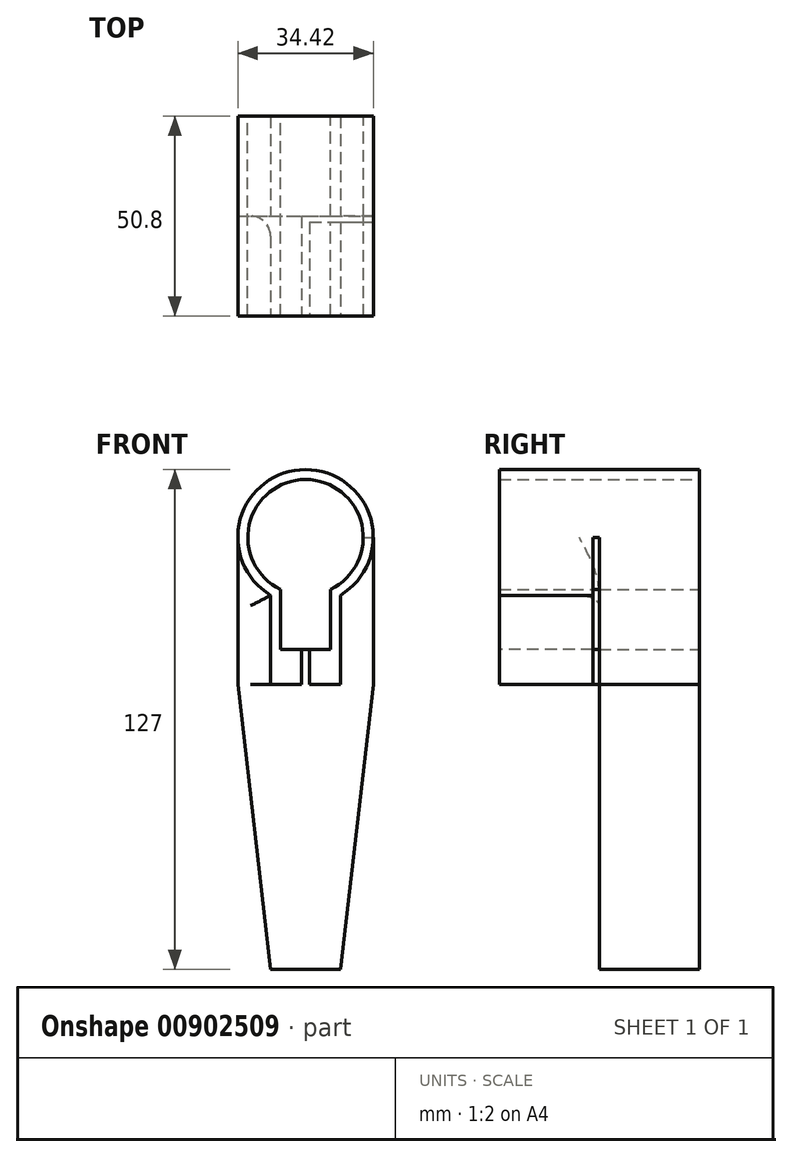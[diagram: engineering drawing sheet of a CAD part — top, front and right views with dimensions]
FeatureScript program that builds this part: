
annotation { "Feature Type Name" : "Feature", "Feature Type Description" : "" }
export const myFeature = defineFeature(function(context is Context, id is Id, definition is map)
    precondition{}
    {
        {
            var Q0;
            Q0=qCreatedBy(makeId("Front.planeOp"),FACE);
            var sketch = newSketch(context, id + "F0", { "sketchPlane" : qUnion([Q0])});
            skLineSegment(sketch, "E0.bottom", {"start": v(-17.2, 17.2) * mm, "end": v(17.2, 17.2) * mm});
            skLineSegment(sketch, "E0.top", {"start": v(-17.2, -109.8) * mm, "end": v(17.2, -109.8) * mm});
            skLineSegment(sketch, "E0.left", {"start": v(-17.2, 17.2) * mm, "end": v(-17.2, -109.8) * mm});
            skLineSegment(sketch, "E0.right", {"start": v(17.2, 17.2) * mm, "end": v(17.2, -109.8) * mm});
            skArc(sketch, "E1", {"start": v(6.35, -13.22) * mm, "mid": v(0, 14.67) * mm, "end": v(-6.35, -13.22) * mm});
            skLineSegment(sketch, "E2.top", {"start": v(-6.35, -28.5) * mm, "end": v(6.35, -28.5) * mm});
            skLineSegment(sketch, "E2.left", {"start": v(-6.35, -13.22) * mm, "end": v(-6.35, -28.5) * mm});
            skLineSegment(sketch, "E2.right", {"start": v(6.35, -13.22) * mm, "end": v(6.35, -28.5) * mm});
            skPoint(sketch, "E3", {"position": v(0, -28.5) * mm});
            skArc(sketch, "E4", {"start": v(6.35, -16) * mm, "mid": v(0, 17.2) * mm, "end": v(-6.35, -16) * mm});
            skSolve(sketch);
        }
        {
            var Q0;
            {var subQ4=sQuery(id+"F0.wireOp",EDGE,"E1");Q0=makeQuery(id+"F0.imprint","IMPRINT",FACE,{"disambiguationData":[TD([[makeQuery(id+"F0.imprint","IMPRINT",EDGE,{"derivedFrom":subQ4}),-1.0]])]});}
            var Q1;
            {var subQ2=sQuery(id+"F0.wireOp",EDGE,"E0.top");Q1=makeQuery(id+"F0.imprint","IMPRINT",FACE,{"disambiguationData":[TD([[makeQuery(id+"F0.imprint","IMPRINT",EDGE,{"derivedFrom":subQ2}),1.0]])]});}
            extrude(context, id + "F1", {"entities" : qUnion([Q0, Q1]), "depth" : 50.8 * mm, "offsetDistance" : 25.4 * mm});
        }
        {
            var Q0;
            Q0=makeQuery(id+"F1.opExtrude","CAP_FACE",FACE,{"disambiguationData":[OSD([sQuery(id+"F0.wireOp",EDGE,"E0.top"),sQuery(id+"F0.wireOp",EDGE,"E0.left"),sQuery(id+"F0.wireOp",EDGE,"E0.right"),sQuery(id+"F0.wireOp",EDGE,"E1"),sQuery(id+"F0.wireOp",EDGE,"E2.top"),sQuery(id+"F0.wireOp",EDGE,"E2.left"),sQuery(id+"F0.wireOp",EDGE,"E2.right"),sQuery(id+"F0.wireOp",EDGE,"E4")])],"isStart":false});
            var sketch = newSketch(context, id + "F2", { "sketchPlane" : qUnion([Q0])});
            skArc(sketch, "E5.0", {"start": v(6.35, -16) * mm, "mid": v(0, 17.2) * mm, "end": v(-6.35, -16) * mm});
            skLineSegment(sketch, "E6", {"start": v(-8.9, -14.73) * mm, "end": v(-8.9, -37.39) * mm});
            skLineSegment(sketch, "E7", {"start": v(-8.9, -37.39) * mm, "end": v(8.9, -37.39) * mm});
            skLineSegment(sketch, "E8", {"start": v(8.9, -37.39) * mm, "end": v(8.9, -14.73) * mm});
            skSolve(sketch);
        }
        {
            var Q0;
            {var subQ0=sQuery(id+"F2.wireOp",EDGE,"E6");Q0=makeQuery(id+"F2.imprint","IMPRINT",FACE,{"disambiguationData":[TD([[makeQuery(id+"F2.imprint","IMPRINT",EDGE,{"derivedFrom":subQ0}),-1.0]])]});}
            extrude(context, id + "F3", {"entities" : qUnion([Q0]), "operationType" : NewBodyOperationType.REMOVE, "oppositeDirection" : true, "depth" : 25.4 * mm, "offsetDistance" : 25.4 * mm});
        }
        {
            var Q0;
            Q0=makeQuery(id+"F1.opExtrude","SWEPT_FACE",FACE,{"disambiguationData":[OSD([sQuery(id+"F0.wireOp",EDGE,"E0.right")])]});
            var sketch = newSketch(context, id + "F4", { "sketchPlane" : qUnion([Q0])});
            skLineSegment(sketch, "E9.bottom", {"start": v(-25.4, 0) * mm, "end": v(-26.99, 0) * mm});
            skLineSegment(sketch, "E9.top", {"start": v(-25.4, -37.39) * mm, "end": v(-26.99, -37.39) * mm});
            skLineSegment(sketch, "E9.left", {"start": v(-25.4, 0) * mm, "end": v(-25.4, -37.39) * mm});
            skLineSegment(sketch, "E9.right", {"start": v(-26.99, 0) * mm, "end": v(-26.99, -37.39) * mm});
            skSolve(sketch);
        }
        {
            var Q0;
            Q0 = qSketchRegion(id + "F4", true);
            var Q1;
            Q1=qCreatedBy(makeId("Right.planeOp"),FACE);
            extrude(context, id + "F5", {"entities" : qUnion([Q0]), "operationType" : NewBodyOperationType.REMOVE, "endBound" : BoundingType.UP_TO_SURFACE, "oppositeDirection" : true, "depth" : 1.16 / 50.8 * mm, "endBoundEntityFace" : qUnion([Q1]), "offsetDistance" : 25.4 * mm});
        }
        {
            var Q0;
            Q0=makeQuery(id+"F1.opExtrude","CAP_FACE",FACE,{"disambiguationData":[OSD([sQuery(id+"F0.wireOp",EDGE,"E0.top"),sQuery(id+"F0.wireOp",EDGE,"E0.left"),sQuery(id+"F0.wireOp",EDGE,"E0.right"),sQuery(id+"F0.wireOp",EDGE,"E1"),sQuery(id+"F0.wireOp",EDGE,"E2.top"),sQuery(id+"F0.wireOp",EDGE,"E2.left"),sQuery(id+"F0.wireOp",EDGE,"E2.right"),sQuery(id+"F0.wireOp",EDGE,"E4")])],"isStart":false});
            var sketch = newSketch(context, id + "F6", { "sketchPlane" : qUnion([Q0])});
            skLineSegment(sketch, "E10.bottom", {"start": v(-1.02, -28.47) * mm, "end": v(1.02, -28.47) * mm});
            skLineSegment(sketch, "E10.top", {"start": v(-1.02, -37.39) * mm, "end": v(1.02, -37.39) * mm});
            skLineSegment(sketch, "E10.left", {"start": v(-1.02, -28.47) * mm, "end": v(-1.02, -37.39) * mm});
            skLineSegment(sketch, "E10.right", {"start": v(1.02, -28.47) * mm, "end": v(1.02, -37.39) * mm});
            skSolve(sketch);
        }
        {
            var Q0;
            Q0 = qSketchRegion(id + "F6", true);
            extrude(context, id + "F7", {"entities" : qUnion([Q0]), "operationType" : NewBodyOperationType.REMOVE, "oppositeDirection" : true, "depth" : 25.4 * mm, "offsetDistance" : 25.4 * mm});
        }
        {
            var Q0;
            Q0=makeQuery(id+"F7.boolean.opBoolean","MERGE",FACE,{"derivedFrom":[makeQuery(id+"F5.boolean.opBoolean","MERGE",FACE,{"derivedFrom":[makeQuery(id+"F3.boolean.opBoolean","COPY",FACE,{"derivedFrom":makeQuery(id+"F3.opExtrude","CAP_FACE",FACE,{"disambiguationData":[OSD([sQuery(id+"F0.wireOp",EDGE,"E0.top"),sQuery(id+"F0.wireOp",EDGE,"E0.left"),sQuery(id+"F0.wireOp",EDGE,"E0.right"),sQuery(id+"F2.wireOp",EDGE,"E5.0"),sQuery(id+"F2.wireOp",EDGE,"E6"),sQuery(id+"F2.wireOp",EDGE,"E7"),sQuery(id+"F2.wireOp",EDGE,"E8")])],"isStart":false})})],"fromTools":[makeQuery(id+"F5.opExtrude","SWEPT_FACE",FACE,{"disambiguationData":[OSD([sQuery(id+"F4.wireOp",EDGE,"E9.left")])]})]})],"fromTools":[makeQuery(id+"F7.opExtrude","CAP_FACE",FACE,{"disambiguationData":[OSD([sQuery(id+"F6.wireOp",EDGE,"E10.bottom"),sQuery(id+"F6.wireOp",EDGE,"E10.top"),sQuery(id+"F6.wireOp",EDGE,"E10.left"),sQuery(id+"F6.wireOp",EDGE,"E10.right")])],"isStart":false})]});
            var sketch = newSketch(context, id + "F8", { "sketchPlane" : qUnion([Q0])});
            skPoint(sketch, "E11.0", {"position": v(8.9, -37.39) * mm});
            skLineSegment(sketch, "E12.bottom", {"start": v(-8.9, -37.39) * mm, "end": v(8.9, -37.39) * mm});
            skLineSegment(sketch, "E12.top", {"start": v(-8.9, -109.8) * mm, "end": v(8.9, -109.8) * mm});
            skLineSegment(sketch, "E12.left", {"start": v(-8.9, -37.39) * mm, "end": v(-8.9, -109.8) * mm});
            skLineSegment(sketch, "E12.right", {"start": v(8.9, -37.39) * mm, "end": v(8.9, -109.8) * mm});
            skLineSegment(sketch, "E13", {"start": v(-17.2, -37.39) * mm, "end": v(-8.9, -109.8) * mm});
            skPoint(sketch, "E14.start.orphan", {"position": v(17.2, -37.39) * mm});
            skLineSegment(sketch, "E15", {"start": v(17.2, -37.39) * mm, "end": v(8.9, -109.8) * mm});
            skSolve(sketch);
        }
        {
            var Q0;
            {var subQ0=sQuery(id+"F8.wireOp",EDGE,"E13");Q0=makeQuery(id+"F8.imprint","IMPRINT",FACE,{"disambiguationData":[TD([[makeQuery(id+"F8.imprint","IMPRINT",EDGE,{"derivedFrom":subQ0}),-1.0]])]});}
            var Q1;
            {var subQ0=sQuery(id+"F8.wireOp",EDGE,"E15");Q1=makeQuery(id+"F8.imprint","IMPRINT",FACE,{"disambiguationData":[TD([[makeQuery(id+"F8.imprint","IMPRINT",EDGE,{"derivedFrom":subQ0}),1.0]])]});}
            extrude(context, id + "F9", {"entities" : qUnion([Q0, Q1]), "operationType" : NewBodyOperationType.REMOVE, "endBound" : BoundingType.THROUGH_ALL, "oppositeDirection" : true, "depth" : 25.4 * mm, "offsetDistance" : 25.4 * mm});
        }
        {
            var Q0;
            Q0=makeQuery(id+"F9.boolean.opBoolean","COPY",EDGE,{"derivedFrom":makeQuery(id+"F9.opExtrude","SWEPT_EDGE",EDGE,{"disambiguationData":[OSD([sQuery(id+"F0.wireOp",EDGE,"E0.top"),sQuery(id+"F8.wireOp",EDGE,"E12.top"),sQuery(id+"F8.wireOp",EDGE,"E12.right"),sQuery(id+"F8.wireOp",EDGE,"E15")])]})});
            var Q1;
            Q1=makeQuery(id+"F9.boolean.opBoolean","COPY",EDGE,{"derivedFrom":makeQuery(id+"F9.opExtrude","SWEPT_EDGE",EDGE,{"disambiguationData":[OSD([sQuery(id+"F0.wireOp",EDGE,"E0.top"),sQuery(id+"F8.wireOp",EDGE,"E12.top"),sQuery(id+"F8.wireOp",EDGE,"E12.left"),sQuery(id+"F8.wireOp",EDGE,"E13")])]})});
            var Q2;
            Q2=makeQuery(id+"F3.boolean.opBoolean","COPY",EDGE,{"derivedFrom":makeQuery(id+"F3.opExtrude","CAP_EDGE",EDGE,{"disambiguationData":[OSD([sQuery(id+"F2.wireOp",EDGE,"E6")])],"isStart":false})});
            var Q3;
            {var subQ0=sQuery(id+"F2.wireOp",EDGE,"E5.0");Q3=makeQuery(id+"F3.boolean.opBoolean","COPY",EDGE,{"derivedFrom":makeQuery(id+"F3.opExtrude","CAP_EDGE",EDGE,{"disambiguationData":[OSD([subQ0]),TDD([makeQuery(id+"F2.imprint","IMPRINT",EDGE,{"disambiguationData":[TD([[makeQuery(id+"F2.imprint","INTERSECT",VERTEX,{"derivedFrom":[makeQuery(id+"F1.opExtrude","CAP_EDGE",EDGE,{"disambiguationData":[OSD([sQuery(id+"F0.wireOp",EDGE,"E0.left")])],"isStart":false}),subQ0]}),-1.0]])],"derivedFrom":subQ0})])],"isStart":false})});}
            fillet(context, id + "F10", {"entities" : qUnion([Q0, Q1, Q2, Q3]), "radius" : 5.08 * mm, "tangentPropagation" : true, "allowEdgeOverflow" : false});
        }
    });
